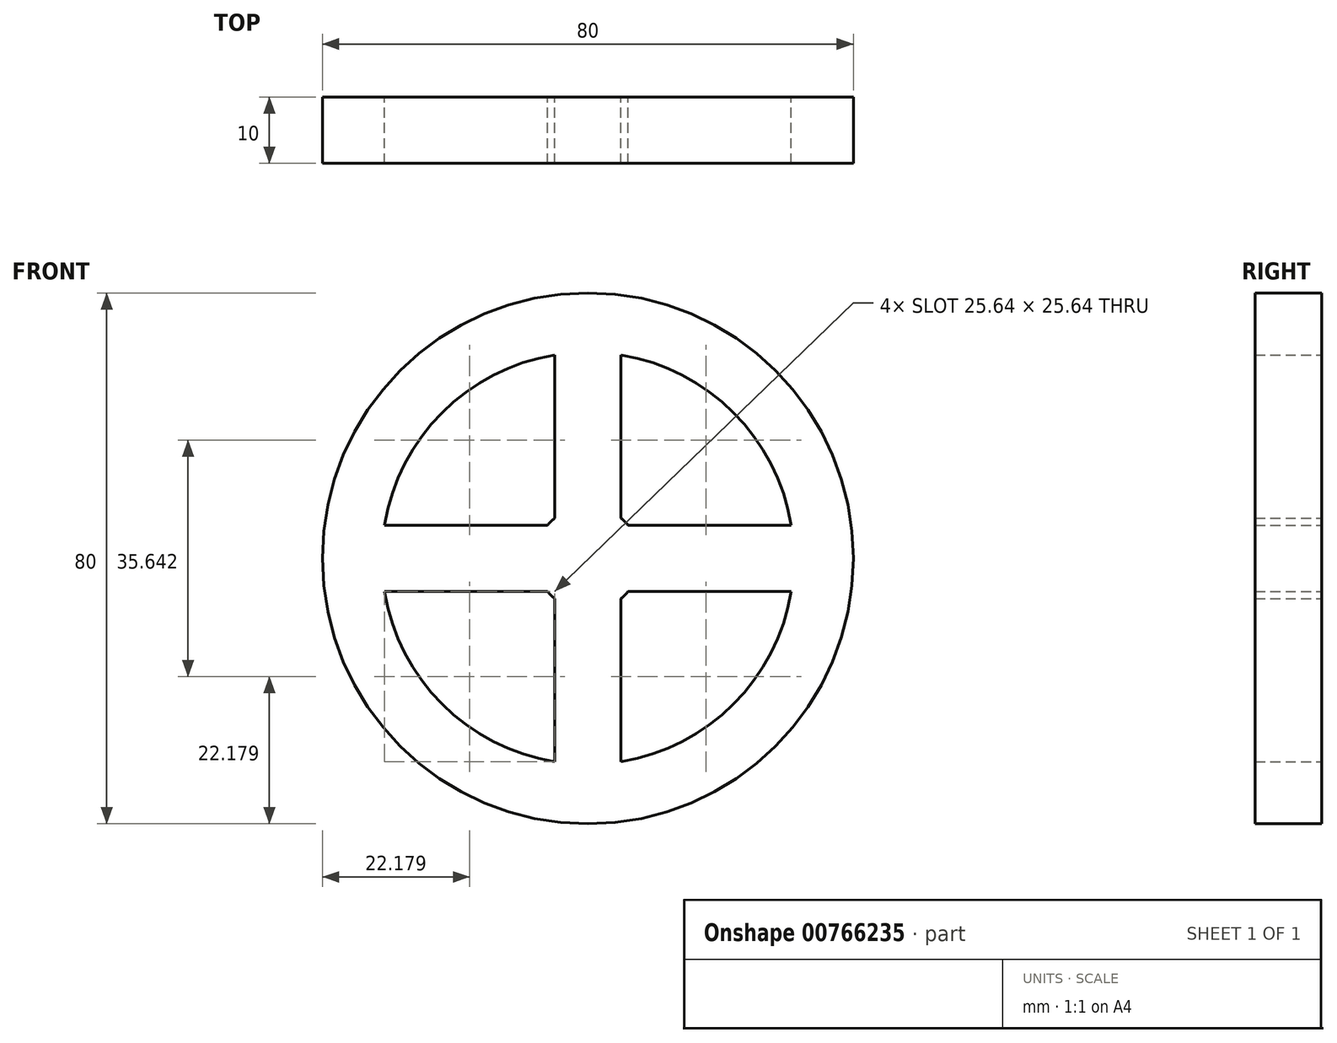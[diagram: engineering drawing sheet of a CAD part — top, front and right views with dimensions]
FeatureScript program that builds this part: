
annotation { "Feature Type Name" : "Feature", "Feature Type Description" : "" }
export const myFeature = defineFeature(function(context is Context, id is Id, definition is map)
    precondition{}
    {
        {
            var Q0;
            Q0=qCreatedBy(makeId("Front.planeOp"),FACE);
            var sketch = newSketch(context, id + "F0", { "sketchPlane" : qUnion([Q0])});
            skCircle(sketch, "E0", {"center": v(0, 0) * mm, "radius": 40 * mm});
            skArc(sketch, "E1", {"start": v(-30.64, -5) * mm, "mid": v(-21.95, -21.95) * mm, "end": v(-5, -30.64) * mm});
            skArc(sketch, "E2", {"start": v(-6.06, -5) * mm, "mid": v(-5.55, -5.55) * mm, "end": v(-5, -6.06) * mm});
            skLineSegment(sketch, "E3.0", {"start": v(5, 40) * mm, "end": v(5, 39.69) * mm});
            skLineSegment(sketch, "E4.0", {"start": v(-5, 40) * mm, "end": v(-5, 39.69) * mm});
            skLineSegment(sketch, "E5.0", {"start": v(-5, -40) * mm, "end": v(-5, -39.69) * mm});
            skLineSegment(sketch, "E6.0", {"start": v(5, -40) * mm, "end": v(5, -39.69) * mm});
            skLineSegment(sketch, "E7.0", {"start": v(-40, -5) * mm, "end": v(-39.69, -5) * mm});
            skLineSegment(sketch, "E8.0", {"start": v(-40, 5) * mm, "end": v(-39.69, 5) * mm});
            skLineSegment(sketch, "E9.0", {"start": v(6.06, -5) * mm, "end": v(30.64, -5) * mm});
            skLineSegment(sketch, "E10.0", {"start": v(6.06, 5) * mm, "end": v(30.64, 5) * mm});
            skLineSegment(sketch, "E11.trimOffspring", {"start": v(-5, 30.64) * mm, "end": v(-5, 6.06) * mm});
            skLineSegment(sketch, "E12.trimOffspring", {"start": v(5, 30.64) * mm, "end": v(5, 6.06) * mm});
            skLineSegment(sketch, "E13.trimOffspring", {"start": v(39.69, 5) * mm, "end": v(40, 5) * mm});
            skLineSegment(sketch, "E14.trimOffspring", {"start": v(39.69, -5) * mm, "end": v(40, -5) * mm});
            skLineSegment(sketch, "E15.trimOffspring", {"start": v(5, -30.64) * mm, "end": v(5, -6.06) * mm});
            skLineSegment(sketch, "E16.trimOffspring", {"start": v(-5, -30.64) * mm, "end": v(-5, -6.06) * mm});
            skLineSegment(sketch, "E17.trimOffspring", {"start": v(-30.64, -5) * mm, "end": v(-6.06, -5) * mm});
            skLineSegment(sketch, "E18.trimOffspring", {"start": v(-30.64, 5) * mm, "end": v(-6.06, 5) * mm});
            skPoint(sketch, "E19.start.orphan", {"position": v(-40, 0) * mm});
            skArc(sketch, "E20.trimOffspring", {"start": v(-5, 30.64) * mm, "mid": v(-21.95, 21.95) * mm, "end": v(-30.64, 5) * mm});
            skArc(sketch, "E21.trimOffspring", {"start": v(30.64, 5) * mm, "mid": v(21.95, 21.95) * mm, "end": v(5, 30.64) * mm});
            skArc(sketch, "E22.trimOffspring", {"start": v(5, -30.64) * mm, "mid": v(21.95, -21.95) * mm, "end": v(30.64, -5) * mm});
            skArc(sketch, "E23.trimOffspring", {"start": v(5, -6.06) * mm, "mid": v(5.55, -5.55) * mm, "end": v(6.06, -5) * mm});
            skArc(sketch, "E24.trimOffspring", {"start": v(6.06, 5) * mm, "mid": v(5.55, 5.55) * mm, "end": v(5, 6.06) * mm});
            skArc(sketch, "E25.trimOffspring", {"start": v(-5, 6.06) * mm, "mid": v(-5.55, 5.55) * mm, "end": v(-6.06, 5) * mm});
            skSolve(sketch);
        }
        {
            var Q0;
            Q0 = qSketchRegion(id + "F0", true);
            extrude(context, id + "F1", {"entities" : qUnion([Q0]), "endBound" : BoundingType.SYMMETRIC, "depth" : 10 * mm, "offsetDistance" : 25 * mm});
        }
    });
